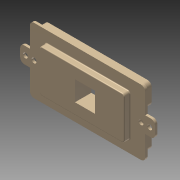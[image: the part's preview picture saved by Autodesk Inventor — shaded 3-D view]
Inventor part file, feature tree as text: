
AUTODESK INVENTOR PART (.ipt)
format: ipt  version: 2015 (Build 190159000, 159)  size: 458,240 bytes
history: native  units: in
note: dims shown in document units (in); Inventor stores cm internally (conversion verified against a paired STEP export)
features: sketch x18, extrude x15, fillet x10, plane x3
ambient origin geometry x8: Origin, YZ Plane, XZ Plane, XY Plane, X Axis, Y Axis, Z Axis, Center Point
bodies: Solid1 (feature_tree)
feature tree (46):
  sketch  "Sketch1"  dims[d7=0.25in d10=4.13in]
  plane  "Work Plane1"
  extrude  "Extrusion2"  Depth=4.13in
  plane  "Work Plane3"
  sketch  "Sketch4"  dims[d22=2.605in d23=1.29in]
  plane  "Work Plane2"
  extrude  "Extrusion8"  Depth=0.075in TaperAngle=0.0deg
  sketch  "Sketch10"  dims[d74=0.15in d75=0.265in d76=0.3in d77=0.75in]
  sketch  "Sketch7"  dims[d37=1.6in d55=2.6in d56=1.3in d68=0.15in]
  extrude  "Extrusion6"  Depth=1.29in
  extrude  "Extrusion7"  Depth=0.1in
  fillet  "Fillet5"  Radius=0.1in
  fillet  "Fillet7"  Radius=0.1in
  fillet  "Fillet8"  Radius=2.8in
  extrude  "Extrusion9"  Depth=2.6in
  fillet  "Fillet11"  Radius=1.3in
  fillet  "Fillet12"  Radius=0.15in
  extrude  "Extrusion17"  Depth=0.2in TaperAngle=0.0deg
  extrude  "Extrusion18"  Depth=0.15in
  extrude  "Extrusion19"  Depth=0.75in
  fillet  "Fillet17"  Radius=0.3in
  fillet  "Fillet20"  Radius=0.75in
  extrude  "Extrusion20"  Depth=0.75in
  fillet  "Fillet18"  Radius=0.3in
  fillet  "Fillet21"  Radius=0.75in
  extrude  "Extrusion21"  Depth=0.125in
  extrude  "Extrusion22"  Depth=0.55in
  extrude  "Extrusion23"  Depth=1.8in
  extrude  "Extrusion24"  Depth=0.25in TaperAngle=0.0deg
  extrude  "Extrusion25"  Depth=0.125in
  extrude  "Extrusion26"  Depth=0.4in
  fillet  "Fillet19"  Radius=0.4in
  sketch  "Sketch2"  dims[d11=2.0in d20=0.075in d21=0.0in]
  sketch  "Sketch5"  dims[d30=0.1in d31=0.1in d32=0.1in d33=0.1in d36=2.8in]
  sketch  "Sketch8"  dims[d69=0.15in d70=0.2in d71=0.0in]
  sketch  "Sketch9"  dims[d72=0.15in d73=0.265in]
  sketch  "Sketch13"  dims[d80=0.3in d81=0.75in d82=0.3in d83=0.75in]
  sketch  "Sketch22"  dims[d84=0.2in d85=0.0in d86=0.125in]
  sketch  "Sketch23"  dims[d89=0.55in d90=0.55in]
  sketch  "Sketch24"  dims[d91=3.28in d92=1.8in]
  sketch  "Sketch25"  dims[d95=0.081in d98=0.25in d99=0.0in]
  sketch  "Sketch26"  dims[d100=0.125in d101=0.125in]
  sketch  "Sketch27"  dims[d107=0.4in d108=0.4in d109=0.4in d110=0.0in]
  sketch  "Sketch28"  dims[d117=0.75in]
  sketch  "Sketch30"  dims[d132=0.1in]
  sketch  "Sketch31"  dims[d133=0.1in d149=0.3in d191=0.25in d192=0.0in d194=0.6102in d195=0.6102in d197=2.04in d198=1.0in d199=0.0in d201=0.06in d202=0.25in d203=0.0in d204=0.05in d205=0.1in d207=0.25in d208=0.0in d209=0.125in d210=0.1in d211=0.0625in d212=0.125in d213=0.0625in d214=0.275in d215=0.275in d216=0.125in d217=0.1625in d218=0.125in d219=0.125in d220=0.1in d221=0.1in d222=0.1in d223=0.075in d224=0.0in d225=1.0in d226=0.0in d227=0.05in d228=0.05in d229=0.05in d230=0.7874in d232=1.9in d233=7.0866in d235=0.202in d238=0.05in d239=6.2992in d241=0.204in d242=0.7874in d244=1.53in d247=0.1in d248=0.0in d249=0.05in d250=3.5433in d252=0.2in d253=0.7874in d255=3.44in d258=0.04in d259=2.7559in d261=0.2in d262=0.7874in d264=3.05in d267=0.1in d268=0.0in d269=0.04in d270=0.7874in d272=3.9in d273=0.7874in d275=0.37in d278=0.2in d279=0.0in d280=0.1in d281=0.5in d282=0.1in d283=0.075in d284=0.0in d285=0.075in d286=0.075in d287=0.025in]
